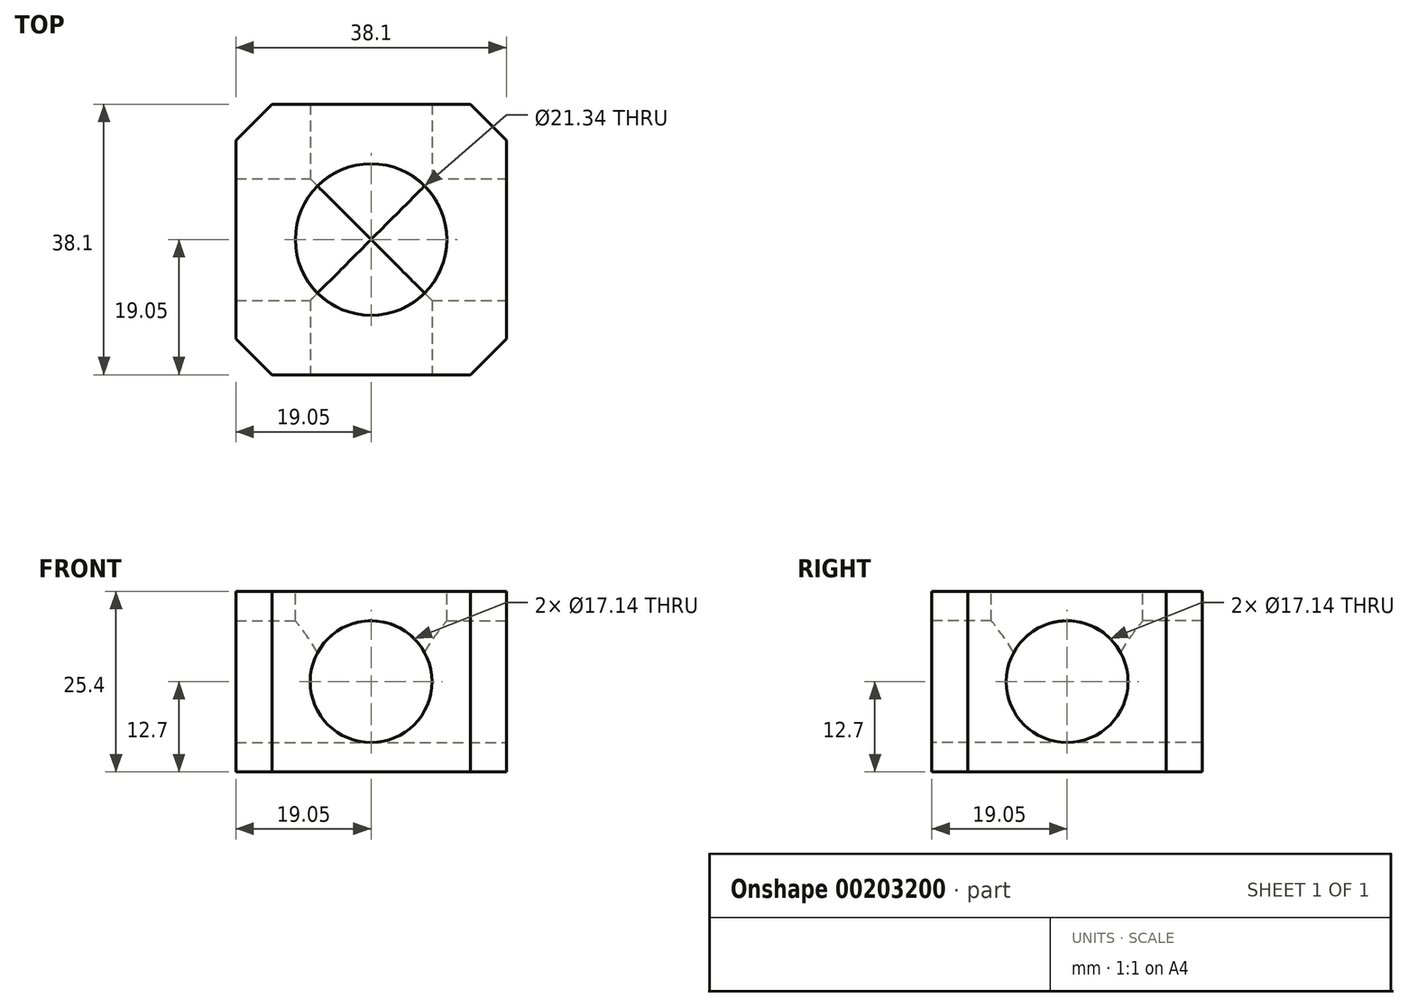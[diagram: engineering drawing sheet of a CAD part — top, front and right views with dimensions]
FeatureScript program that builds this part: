
annotation { "Feature Type Name" : "Feature", "Feature Type Description" : "" }
export const myFeature = defineFeature(function(context is Context, id is Id, definition is map)
    precondition{}
    {
        {
            var Q0;
            Q0=qCreatedBy(makeId("Top.planeOp"),FACE);
            var sketch = newSketch(context, id + "F0", { "sketchPlane" : qUnion([Q0])});
            skLineSegment(sketch, "E0.bottom", {"start": v(19.05, -19.05) * mm, "end": v(-19.05, -19.05) * mm});
            skLineSegment(sketch, "E0.top", {"start": v(19.05, 19.05) * mm, "end": v(-19.05, 19.05) * mm});
            skLineSegment(sketch, "E0.left", {"start": v(19.05, -19.05) * mm, "end": v(19.05, 19.05) * mm});
            skLineSegment(sketch, "E0.right", {"start": v(-19.05, -19.05) * mm, "end": v(-19.05, 19.05) * mm});
            skPoint(sketch, "E0.middle", {"position": v(0, 0) * mm});
            skSolve(sketch);
        }
        {
            var Q0;
            Q0 = qSketchRegion(id + "F0", true);
            extrude(context, id + "F1", {"entities" : qUnion([Q0]), "depth" : 25.4 * mm});
        }
        {
            var Q0;
            Q0=makeQuery(id+"F1.opExtrude","CAP_FACE",FACE,{"disambiguationData":[OSD([sQuery(id+"F0.wireOp",EDGE,"E0.bottom"),sQuery(id+"F0.wireOp",EDGE,"E0.top"),sQuery(id+"F0.wireOp",EDGE,"E0.left"),sQuery(id+"F0.wireOp",EDGE,"E0.right")])],"isStart":false});
            var sketch = newSketch(context, id + "F2", { "sketchPlane" : qUnion([Q0])});
            skCircle(sketch, "E1", {"center": v(0, 0) * mm, "radius": 10.67 * mm});
            skSolve(sketch);
        }
        {
            var Q0;
            Q0=makeQuery(id+"F1.opExtrude","SWEPT_FACE",FACE,{"disambiguationData":[OSD([sQuery(id+"F0.wireOp",EDGE,"E0.bottom")])]});
            var sketch = newSketch(context, id + "F3", { "sketchPlane" : qUnion([Q0])});
            skLineSegment(sketch, "E2", {"start": v(0, 0) * mm, "end": v(0, 25.4) * mm});
            skLineSegment(sketch, "E3", {"start": v(0, 25.4) * mm, "end": v(0, 12.7) * mm});
            skCircle(sketch, "E4", {"center": v(0, 12.7) * mm, "radius": 8.57 * mm});
            skSolve(sketch);
        }
        {
            var Q0;
            Q0 = qSketchRegion(id + "F3", true);
            extrude(context, id + "F4", {"entities" : qUnion([Q0]), "operationType" : NewBodyOperationType.REMOVE, "oppositeDirection" : true, "depth" : 76.2 * mm});
        }
        {
            var Q0;
            Q0=makeQuery(id+"F1.opExtrude","SWEPT_FACE",FACE,{"disambiguationData":[OSD([sQuery(id+"F0.wireOp",EDGE,"E0.left")])]});
            var sketch = newSketch(context, id + "F5", { "sketchPlane" : qUnion([Q0])});
            skLineSegment(sketch, "E5", {"start": v(0, 0) * mm, "end": v(0, 25.4) * mm});
            skLineSegment(sketch, "E6", {"start": v(0, 25.4) * mm, "end": v(0, 12.7) * mm});
            skCircle(sketch, "E7", {"center": v(0, 12.7) * mm, "radius": 8.57 * mm});
            skSolve(sketch);
        }
        {
            var Q0;
            Q0 = qSketchRegion(id + "F5", true);
            extrude(context, id + "F6", {"entities" : qUnion([Q0]), "operationType" : NewBodyOperationType.REMOVE, "oppositeDirection" : true, "depth" : 76.2 * mm});
        }
        {
            var Q0;
            Q0=makeQuery(id+"F2.imprint","IMPRINT",FACE,{"disambiguationData":[TD([[makeQuery(id+"F2.imprint","IMPRINT",EDGE,{"derivedFrom":sQuery(id+"F2.wireOp",EDGE,"E1")}),1.0]])]});
            extrude(context, id + "F7", {"entities" : qUnion([Q0]), "operationType" : NewBodyOperationType.REMOVE, "oppositeDirection" : true, "depth" : 12.7 * mm});
        }
        {
            var Q0;
            Q0=makeQuery(id+"F1.opExtrude","SWEPT_EDGE",EDGE,{"disambiguationData":[OSD([sQuery(id+"F0.wireOp",EDGE,"E0.top"),sQuery(id+"F0.wireOp",EDGE,"E0.right")])]});
            var Q1;
            Q1=makeQuery(id+"F1.opExtrude","SWEPT_EDGE",EDGE,{"disambiguationData":[OSD([sQuery(id+"F0.wireOp",EDGE,"E0.top"),sQuery(id+"F0.wireOp",EDGE,"E0.left")])]});
            var Q2;
            Q2=makeQuery(id+"F1.opExtrude","SWEPT_EDGE",EDGE,{"disambiguationData":[OSD([sQuery(id+"F0.wireOp",EDGE,"E0.bottom"),sQuery(id+"F0.wireOp",EDGE,"E0.left")])]});
            var Q3;
            Q3=makeQuery(id+"F1.opExtrude","SWEPT_EDGE",EDGE,{"disambiguationData":[OSD([sQuery(id+"F0.wireOp",EDGE,"E0.bottom"),sQuery(id+"F0.wireOp",EDGE,"E0.right")])]});
            chamfer(context, id + "F8", {"entities" : qUnion([Q0, Q1, Q2, Q3]), "width" : 5.08 * mm, "tangentPropagation" : true});
        }
    });
